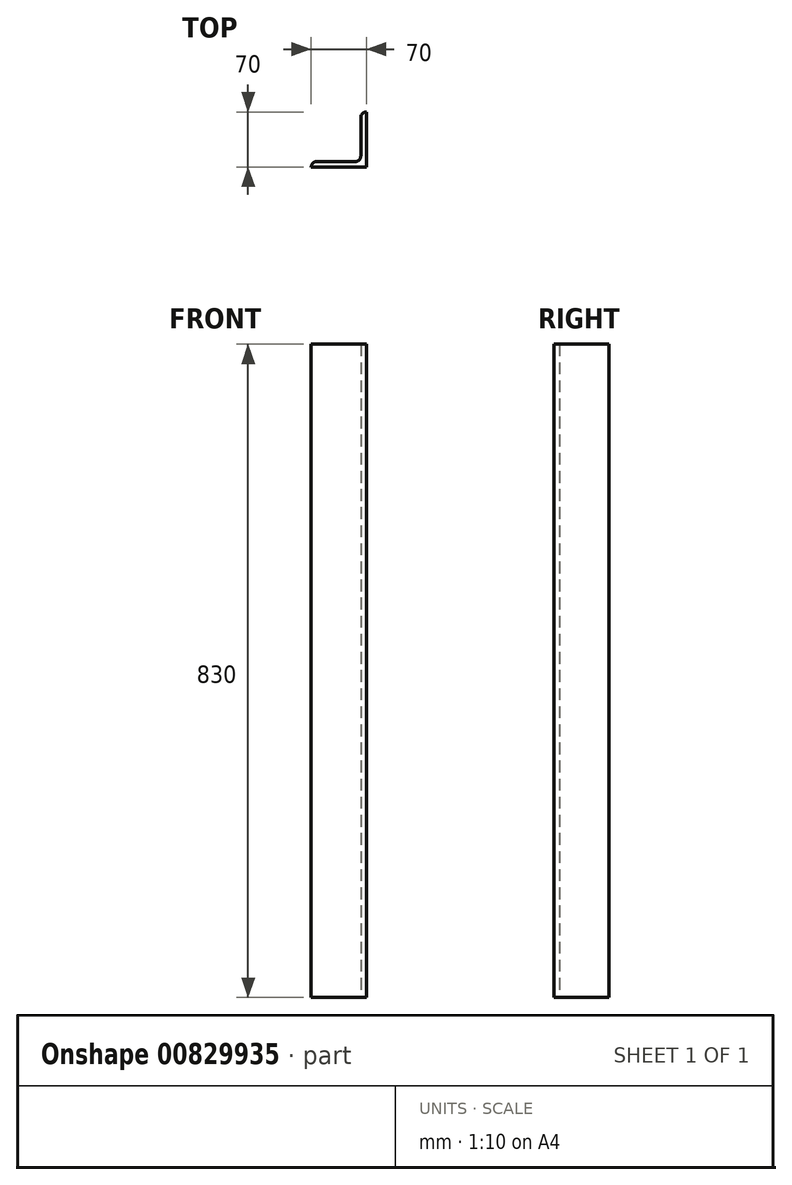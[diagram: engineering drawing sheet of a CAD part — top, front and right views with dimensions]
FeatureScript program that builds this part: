
annotation { "Feature Type Name" : "Feature", "Feature Type Description" : "" }
export const myFeature = defineFeature(function(context is Context, id is Id, definition is map)
    precondition{}
    {
        {
            var Q0;
            Q0=qCreatedBy(makeId("Top.planeOp"),FACE);
            var sketch = newSketch(context, id + "F0", { "sketchPlane" : qUnion([Q0])});
            skLineSegment(sketch, "E0", {"start": v(0, 0) * mm, "end": v(0, 70) * mm});
            skLineSegment(sketch, "E1", {"start": v(0, 0) * mm, "end": v(-70, 0) * mm});
            skLineSegment(sketch, "E2", {"start": v(-70, 0) * mm, "end": v(-70, 0) * mm});
            skLineSegment(sketch, "E3", {"start": v(-63, 7) * mm, "end": v(-14, 7) * mm});
            skLineSegment(sketch, "E4", {"start": v(-7, 14) * mm, "end": v(-7, 63) * mm});
            skLineSegment(sketch, "E5", {"start": v(0, 70) * mm, "end": v(0, 70) * mm});
            skPoint(sketch, "E6.visualSharp", {"position": v(-70, 7) * mm});
            skArc(sketch, "E6.filletArc", {"start": v(-63, 7) * mm, "mid": v(-67.95, 4.95) * mm, "end": v(-70, 0) * mm});
            skPoint(sketch, "E7.visualSharp", {"position": v(-7, 70) * mm});
            skArc(sketch, "E7.filletArc", {"start": v(0, 70) * mm, "mid": v(-4.95, 67.95) * mm, "end": v(-7, 63) * mm});
            skPoint(sketch, "E8.visualSharp", {"position": v(-7, 7) * mm});
            skArc(sketch, "E8.filletArc", {"start": v(-14, 7) * mm, "mid": v(-9.05, 9.05) * mm, "end": v(-7, 14) * mm});
            skSolve(sketch);
        }
        {
            var Q0;
            Q0=makeQuery(id+"F0.imprint","IMPRINT",FACE,{"disambiguationData":[TD([[makeQuery(id+"F0.imprint","IMPRINT",EDGE,{"derivedFrom":sQuery(id+"F0.wireOp",EDGE,"E0")}),1.0]])]});
            extrude(context, id + "F1", {"entities" : qUnion([Q0]), "depth" : 830 * mm, "offsetDistance" : 25 * mm});
        }
    });
